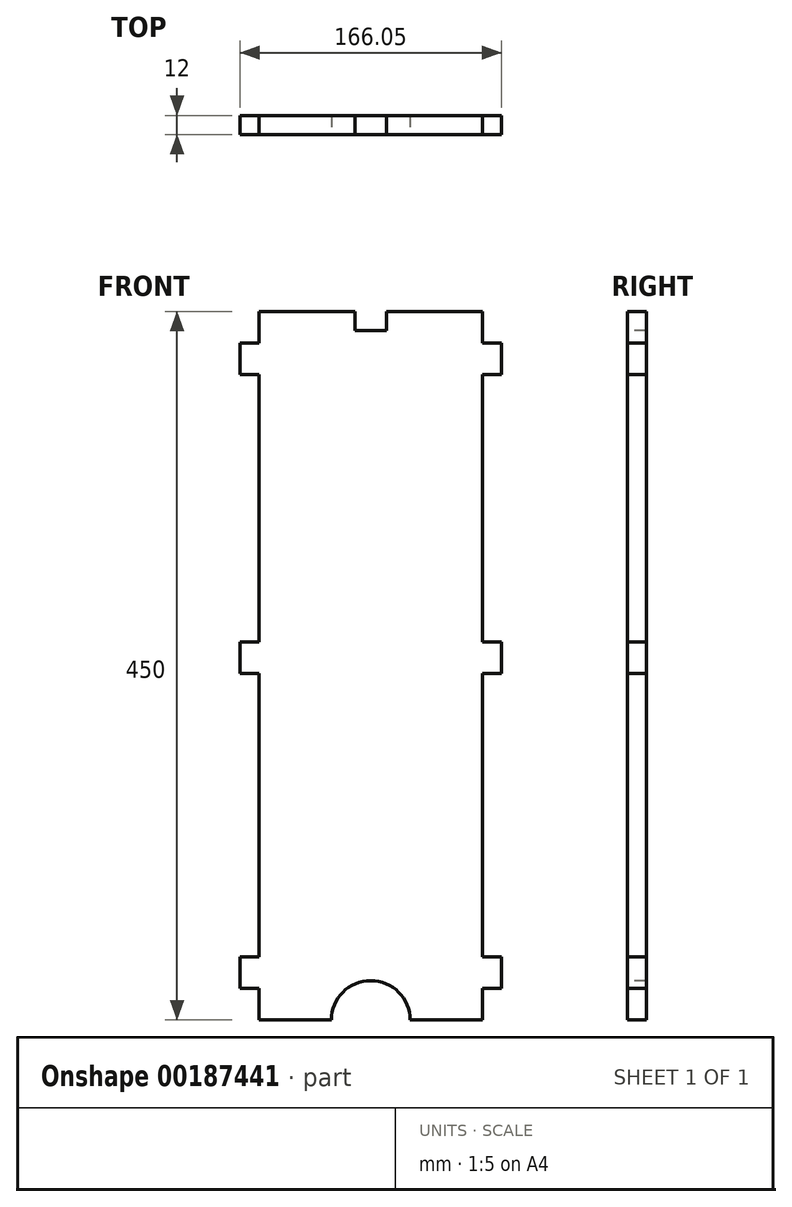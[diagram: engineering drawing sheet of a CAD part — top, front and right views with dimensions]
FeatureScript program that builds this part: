
annotation { "Feature Type Name" : "Feature", "Feature Type Description" : "" }
export const myFeature = defineFeature(function(context is Context, id is Id, definition is map)
    precondition{}
    {
        {
            var Q0;
            Q0=qCreatedBy(makeId("Front.planeOp"),FACE);
            var sketch = newSketch(context, id + "F0", { "sketchPlane" : qUnion([Q0])});
            skLineSegment(sketch, "E0.bottom", {"start": v(0, 0) * mm, "end": v(142.05, 0) * mm});
            skLineSegment(sketch, "E0.top", {"start": v(0, 460) * mm, "end": v(142.05, 460) * mm});
            skLineSegment(sketch, "E0.left", {"start": v(0, 0) * mm, "end": v(0, 460) * mm});
            skLineSegment(sketch, "E0.right", {"start": v(142.05, 0) * mm, "end": v(142.05, 460) * mm});
            skSolve(sketch);
        }
        {
            var Q0;
            Q0 = qSketchRegion(id + "F0", true);
            extrude(context, id + "F1", {"entities" : qUnion([Q0]), "depth" : 12 * mm});
        }
        {
            var Q0;
            Q0=makeQuery(id+"F1.opExtrude","CAP_FACE",FACE,{"disambiguationData":[OSD([sQuery(id+"F0.wireOp",EDGE,"E0.bottom"),sQuery(id+"F0.wireOp",EDGE,"E0.top"),sQuery(id+"F0.wireOp",EDGE,"E0.left"),sQuery(id+"F0.wireOp",EDGE,"E0.right")])],"isStart":false});
            var sketch = newSketch(context, id + "F2", { "sketchPlane" : qUnion([Q0])});
            skLineSegment(sketch, "E1", {"start": v(71.02, 460) * mm, "end": v(71.02, 448.65) * mm});
            skPoint(sketch, "E1.endSnap0", {"position": v(71.02, 460) * mm});
            skLineSegment(sketch, "E2.bottom", {"start": v(0, 430) * mm, "end": v(-10, 430) * mm});
            skLineSegment(sketch, "E2.top", {"start": v(0, 410) * mm, "end": v(-10, 410) * mm});
            skLineSegment(sketch, "E2.left", {"start": v(0, 430) * mm, "end": v(0, 410) * mm});
            skLineSegment(sketch, "E2.right", {"start": v(-10, 430) * mm, "end": v(-10, 410) * mm});
            skLineSegment(sketch, "E3.bottom", {"start": v(0, 240) * mm, "end": v(-10, 240) * mm});
            skLineSegment(sketch, "E3.top", {"start": v(0, 220) * mm, "end": v(-10, 220) * mm});
            skLineSegment(sketch, "E3.left", {"start": v(0, 240) * mm, "end": v(0, 220) * mm});
            skLineSegment(sketch, "E3.right", {"start": v(-10, 240) * mm, "end": v(-10, 220) * mm});
            skLineSegment(sketch, "E4.MirrorCS", {"start": v(0, 20) * mm, "end": v(-10, 20) * mm});
            skLineSegment(sketch, "E5.MirrorCS", {"start": v(-10, 20) * mm, "end": v(-10, 40) * mm});
            skLineSegment(sketch, "E6.MirrorCS", {"start": v(0, 40) * mm, "end": v(-10, 40) * mm});
            skLineSegment(sketch, "E7.MirrorCS", {"start": v(152.05, 430) * mm, "end": v(152.05, 410) * mm});
            skLineSegment(sketch, "E8.MirrorCS", {"start": v(142.05, 430) * mm, "end": v(142.05, 410) * mm});
            skLineSegment(sketch, "E9.MirrorCS", {"start": v(142.05, 430) * mm, "end": v(152.05, 430) * mm});
            skLineSegment(sketch, "E10.MirrorCS", {"start": v(142.05, 410) * mm, "end": v(152.05, 410) * mm});
            skLineSegment(sketch, "E11.MirrorCS", {"start": v(142.05, 240) * mm, "end": v(152.05, 240) * mm});
            skLineSegment(sketch, "E12.MirrorCS", {"start": v(142.05, 220) * mm, "end": v(152.05, 220) * mm});
            skLineSegment(sketch, "E13.MirrorCS", {"start": v(142.05, 240) * mm, "end": v(142.05, 220) * mm});
            skLineSegment(sketch, "E14.MirrorCS", {"start": v(152.05, 240) * mm, "end": v(152.05, 220) * mm});
            skLineSegment(sketch, "E15.MirrorCS", {"start": v(142.05, 20) * mm, "end": v(152.05, 20) * mm});
            skLineSegment(sketch, "E16.MirrorCS", {"start": v(152.05, 20) * mm, "end": v(152.05, 40) * mm});
            skLineSegment(sketch, "E17.MirrorCS", {"start": v(142.05, 40) * mm, "end": v(152.05, 40) * mm});
            skLineSegment(sketch, "E18.bottom", {"start": v(81.02, 480) * mm, "end": v(61.02, 480) * mm});
            skLineSegment(sketch, "E18.top", {"start": v(81.02, 440) * mm, "end": v(61.02, 440) * mm});
            skLineSegment(sketch, "E18.left", {"start": v(81.02, 480) * mm, "end": v(81.02, 440) * mm});
            skLineSegment(sketch, "E18.right", {"start": v(61.02, 480) * mm, "end": v(61.02, 440) * mm});
            skSolve(sketch);
        }
        {
            var Q0;
            Q0=makeQuery(id+"F2.imprint","IMPRINT",FACE,{"disambiguationData":[TD([[makeQuery(id+"F2.imprint","IMPRINT",EDGE,{"derivedFrom":sQuery(id+"F2.wireOp",EDGE,"E2.bottom")}),1.0]])]});
            var Q1;
            Q1=makeQuery(id+"F2.imprint","IMPRINT",FACE,{"disambiguationData":[TD([[makeQuery(id+"F2.imprint","IMPRINT",EDGE,{"derivedFrom":sQuery(id+"F2.wireOp",EDGE,"E7.MirrorCS")}),-1.0]])]});
            var Q2;
            {var subQ2=sQuery(id+"F2.wireOp",EDGE,"E3.bottom");Q2=makeQuery(id+"F2.imprint","IMPRINT",FACE,{"disambiguationData":[TD([[makeQuery(id+"F2.imprint","IMPRINT",EDGE,{"derivedFrom":subQ2}),1.0]])]});}
            var Q3;
            Q3=makeQuery(id+"F2.imprint","IMPRINT",FACE,{"disambiguationData":[TD([[makeQuery(id+"F2.imprint","IMPRINT",EDGE,{"derivedFrom":sQuery(id+"F2.wireOp",EDGE,"E11.MirrorCS")}),-1.0]])]});
            var Q4;
            {var subQ0=sQuery(id+"F2.wireOp",EDGE,"E4.MirrorCS");Q4=makeQuery(id+"F2.imprint","IMPRINT",FACE,{"disambiguationData":[TD([[makeQuery(id+"F2.imprint","IMPRINT",EDGE,{"derivedFrom":subQ0}),-1.0]])]});}
            var Q5;
            {var subQ0=sQuery(id+"F2.wireOp",EDGE,"E15.MirrorCS");Q5=makeQuery(id+"F2.imprint","IMPRINT",FACE,{"disambiguationData":[TD([[makeQuery(id+"F2.imprint","IMPRINT",EDGE,{"derivedFrom":subQ0}),1.0]])]});}
            extrude(context, id + "F3", {"entities" : qUnion([Q0, Q1, Q2, Q3, Q4, Q5]), "operationType" : NewBodyOperationType.ADD, "oppositeDirection" : true, "depth" : 12 * mm});
        }
        {
            var Q0;
            {var subQ5=sQuery(id+"F2.wireOp",EDGE,"E18.bottom");Q0=makeQuery(id+"F2.imprint","IMPRINT",FACE,{"disambiguationData":[TD([[makeQuery(id+"F2.imprint","IMPRINT",EDGE,{"derivedFrom":subQ5}),1.0]])]});}
            var Q1;
            {var subQ5=sQuery(id+"F2.wireOp",EDGE,"E18.top");Q1=makeQuery(id+"F2.imprint","IMPRINT",FACE,{"disambiguationData":[TD([[makeQuery(id+"F2.imprint","IMPRINT",EDGE,{"derivedFrom":subQ5}),-1.0]])]});}
            extrude(context, id + "F4", {"entities" : qUnion([Q0, Q1]), "operationType" : NewBodyOperationType.REMOVE, "oppositeDirection" : true, "depth" : 25 * mm, "offsetDistance" : 25 * mm});
        }
        {
            var Q0;
            Q0=makeQuery(id+"F4.boolean.opBoolean","COPY",FACE,{"derivedFrom":makeQuery(id+"F4.opExtrude","SWEPT_FACE",FACE,{"disambiguationData":[OSD([sQuery(id+"F2.wireOp",EDGE,"E18.top")])]})});
            extrude(context, id + "F5", {"entities" : qUnion([Q0]), "operationType" : NewBodyOperationType.REMOVE, "oppositeDirection" : true, "depth" : 2 * mm});
        }
        {
            var Q0;
            {var subQ0=sQuery(id+"F0.wireOp",EDGE,"E0.right");var subQ1=sQuery(id+"F0.wireOp",EDGE,"E0.left");Q0=makeQuery(id+"F3.boolean.opBoolean","MERGE",FACE,{"derivedFrom":[makeQuery(id+"F1.opExtrude","CAP_FACE",FACE,{"disambiguationData":[OSD([sQuery(id+"F0.wireOp",EDGE,"E0.bottom"),sQuery(id+"F0.wireOp",EDGE,"E0.top"),subQ1,subQ0])],"isStart":false}),makeQuery(id+"F3.opExtrude","CAP_FACE",FACE,{"disambiguationData":[OSD([sQuery(id+"F2.wireOp",EDGE,"E2.bottom"),sQuery(id+"F2.wireOp",EDGE,"E2.top"),sQuery(id+"F2.wireOp",EDGE,"E2.left"),sQuery(id+"F2.wireOp",EDGE,"E2.right")])],"isStart":true}),makeQuery(id+"F3.opExtrude","CAP_FACE",FACE,{"disambiguationData":[OSD([sQuery(id+"F2.wireOp",EDGE,"E3.bottom"),sQuery(id+"F2.wireOp",EDGE,"E3.top"),sQuery(id+"F2.wireOp",EDGE,"E3.left"),sQuery(id+"F2.wireOp",EDGE,"E3.right")])],"isStart":true}),makeQuery(id+"F3.opExtrude","CAP_FACE",FACE,{"disambiguationData":[OSD([subQ1,sQuery(id+"F2.wireOp",EDGE,"E4.MirrorCS"),sQuery(id+"F2.wireOp",EDGE,"E5.MirrorCS"),sQuery(id+"F2.wireOp",EDGE,"E6.MirrorCS")])],"isStart":true}),makeQuery(id+"F3.opExtrude","CAP_FACE",FACE,{"disambiguationData":[OSD([sQuery(id+"F2.wireOp",EDGE,"E7.MirrorCS"),sQuery(id+"F2.wireOp",EDGE,"E8.MirrorCS"),sQuery(id+"F2.wireOp",EDGE,"E9.MirrorCS"),sQuery(id+"F2.wireOp",EDGE,"E10.MirrorCS")])],"isStart":true}),makeQuery(id+"F3.opExtrude","CAP_FACE",FACE,{"disambiguationData":[OSD([sQuery(id+"F2.wireOp",EDGE,"E11.MirrorCS"),sQuery(id+"F2.wireOp",EDGE,"E12.MirrorCS"),sQuery(id+"F2.wireOp",EDGE,"E13.MirrorCS"),sQuery(id+"F2.wireOp",EDGE,"E14.MirrorCS")])],"isStart":true}),makeQuery(id+"F3.opExtrude","CAP_FACE",FACE,{"disambiguationData":[OSD([subQ0,sQuery(id+"F2.wireOp",EDGE,"E15.MirrorCS"),sQuery(id+"F2.wireOp",EDGE,"E16.MirrorCS"),sQuery(id+"F2.wireOp",EDGE,"E17.MirrorCS")])],"isStart":true})]});}
            var sketch = newSketch(context, id + "F6", { "sketchPlane" : qUnion([Q0])});
            skCircle(sketch, "E19", {"center": v(71.03, 0) * mm, "radius": 25 * mm});
            skSolve(sketch);
        }
        {
            var Q0;
            {var subQ0=sQuery(id+"F6.wireOp",EDGE,"E19");var subQ1=makeQuery(id+"F1.opExtrude","CAP_EDGE",EDGE,{"disambiguationData":[OSD([sQuery(id+"F0.wireOp",EDGE,"E0.bottom")])],"isStart":false});var subQ2=makeQuery(id+"F6.imprint","INTERSECT",VERTEX,{"disambiguationData":[OD(0.0)],"derivedFrom":[subQ1,subQ0]});Q0=makeQuery(id+"F6.imprint","IMPRINT",FACE,{"disambiguationData":[TD([[makeQuery(id+"F6.imprint","IMPRINT",EDGE,{"disambiguationData":[TD([[subQ2,1.0]])],"derivedFrom":subQ0}),1.0]])]});}
            extrude(context, id + "F7", {"entities" : qUnion([Q0]), "operationType" : NewBodyOperationType.REMOVE, "oppositeDirection" : true, "depth" : 25 * mm, "offsetDistance" : 25 * mm});
        }
        {
            var Q0;
            {var subQ15=sQuery(id+"F0.wireOp",EDGE,"E0.left");var subQ24=sQuery(id+"F0.wireOp",EDGE,"E0.top");Q0=makeQuery(id+"F4.boolean.opBoolean","SPLIT",FACE,{"disambiguationData":[TD([makeQuery(id+"F1.opExtrude","SWEPT_FACE",FACE,{"disambiguationData":[OSD([subQ15])]})])],"derivedFrom":makeQuery(id+"F1.opExtrude","SWEPT_FACE",FACE,{"disambiguationData":[OSD([subQ24])]})});}
            var Q1;
            {var subQ11=sQuery(id+"F0.wireOp",EDGE,"E0.right");var subQ24=sQuery(id+"F0.wireOp",EDGE,"E0.top");Q1=makeQuery(id+"F4.boolean.opBoolean","SPLIT",FACE,{"disambiguationData":[TD([makeQuery(id+"F1.opExtrude","SWEPT_FACE",FACE,{"disambiguationData":[OSD([subQ11])]})])],"derivedFrom":makeQuery(id+"F1.opExtrude","SWEPT_FACE",FACE,{"disambiguationData":[OSD([subQ24])]})});}
            extrude(context, id + "F8", {"entities" : qUnion([Q0, Q1]), "operationType" : NewBodyOperationType.REMOVE, "oppositeDirection" : true, "depth" : 10 * mm, "offsetDistance" : 25 * mm});
        }
        {
            var Q0;
            Q0=makeQuery(id+"F3.opExtrude","SWEPT_FACE",FACE,{"disambiguationData":[OSD([sQuery(id+"F2.wireOp",EDGE,"E7.MirrorCS")])]});
            var Q1;
            Q1=makeQuery(id+"F3.opExtrude","SWEPT_FACE",FACE,{"disambiguationData":[OSD([sQuery(id+"F2.wireOp",EDGE,"E14.MirrorCS")])]});
            var Q2;
            Q2=makeQuery(id+"F3.opExtrude","SWEPT_FACE",FACE,{"disambiguationData":[OSD([sQuery(id+"F2.wireOp",EDGE,"E16.MirrorCS")])]});
            extrude(context, id + "F9", {"entities" : qUnion([Q0, Q1, Q2]), "operationType" : NewBodyOperationType.ADD, "depth" : 2 * mm, "offsetDistance" : 25 * mm});
        }
        {
            var Q0;
            Q0=makeQuery(id+"F3.opExtrude","SWEPT_FACE",FACE,{"disambiguationData":[OSD([sQuery(id+"F2.wireOp",EDGE,"E2.right")])]});
            var Q1;
            Q1=makeQuery(id+"F3.opExtrude","SWEPT_FACE",FACE,{"disambiguationData":[OSD([sQuery(id+"F2.wireOp",EDGE,"E3.right")])]});
            var Q2;
            Q2=makeQuery(id+"F3.opExtrude","SWEPT_FACE",FACE,{"disambiguationData":[OSD([sQuery(id+"F2.wireOp",EDGE,"E5.MirrorCS")])]});
            extrude(context, id + "F10", {"entities" : qUnion([Q0, Q1, Q2]), "operationType" : NewBodyOperationType.ADD, "depth" : 2 * mm, "offsetDistance" : 25 * mm});
        }
    });
